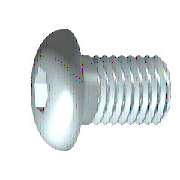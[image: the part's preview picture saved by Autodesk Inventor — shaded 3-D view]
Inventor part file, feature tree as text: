
AUTODESK INVENTOR PART (.ipt)
format: ipt  version: 2015 (Build 190159000, 159)  size: 200,704 bytes
history: native  units: mm (DEFAULTED — no unit token found)
features: sketch x2, extrude x1, plane x1, fillet x1
ambient origin geometry x7: Origin, YZ Plane, XY Plane, X Axis, Y Axis, Z Axis, Center Point
bodies: Solid1 (feature_tree), Body (feature_tree)
feature tree (5):
  extrude  "Slot"  Depth=3.3528mm
  plane  "Work Plane1"
  fillet  "Fillet2"  Radius=3.3528mm
  sketch  "Sketch1"  dims[d1=10.1598mm d2=2.5401mm d3=3.3528mm]
  sketch  "Sketch2"  dims[d4=2.2098mm d5=60.0deg d6=6.35mm d7=6.35mm d8=4.575385mm d9=11.0998mm d10=90.0deg d11=10.0mm d12=0.0mm d13=10.1598mm d14=0.0mm d15=0.779018mm d16=0.779018mm d17=2.9718mm d19=0.0mm d26=12.7mm d27=45.0deg d28=0.0mm d29=0.0mm d30=0.1mm]
